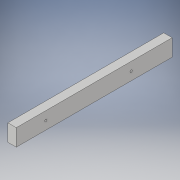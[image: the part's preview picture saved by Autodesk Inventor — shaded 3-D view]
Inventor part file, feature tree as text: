
AUTODESK INVENTOR PART (.ipt)
format: ipt  version: 2019.1 (Build 231200000, 200)  size: 107,008 bytes
history: native  units: in
note: dims shown in document units (in); Inventor stores cm internally (conversion verified against a paired STEP export)
features: extrude x2, sketch x2
ambient origin geometry x8: Origin, YZ Plane, XZ Plane, XY Plane, X Axis, Y Axis, Z Axis, Center Point
bodies: Solid1 (feature_tree)
feature tree (4):
  extrude  "Extrusion1"  Depth=18.5in
  extrude  "Extrusion2"  Depth=2.0in
  sketch  "Sketch1"  dims[d0=1.0in d1=18.5in]
  sketch  "Sketch5"  dims[d2=2.0in d3=0.0in d18=10.125in d20=0.266in d21=0.266in d22=2.0in d23=0.0in d24=3.5in]
